# Revit family: 1000811 Font Uber 2 SS Button Tile L&R
name_source: partatom
category: Generic Models
revit_build: Autodesk Revit 2015 (Build: 20160512_1515(x64)
units: mm (PartAtom-declared; Revit-internal decimal feet)

## types (1)
- 1000811 Font Uber 2 SS Button Tile L&R
    Arrangement = Counter Mounted
    AssetType = Fixed
    Color = Brushed Stainless Steel
    ConstructionCasingFinish = Brushed
    ConstructionCasingMaterial = Stainless Steel
    Default Elevation = 1219 mm
    Depth = 360 mm
    Description = Marco Uber style font to be used with Marco Ecoboiler Under counter boilers
    DimensionsDepthMaximum = 470mm
    DimensionsHeightMaximum = 400mm
    DimensionsWidthMaximum = 250mm
    DurationUnit = 5-Years
    ExpectedLife = 5-Years
    H = 272 mm
    Manufacturer = Marco Beverage Systems Ltd.
    Material = Stainless Steel
    ModelNumber = 1000811
    ModelReference = Font Uber 2 SS Button Tile L&R
    Standard = EN 60335-2-75
    ThirdPartyAccreditation = UL, NSF
    URL = http://marcobeveragesystems.com
    WarrantyDescription = Parts Only
    WarrantyDurationLabor = 0
    WarrantyDurationParts = 2-years
    WarrantyDurationUnit = 2-years
    WaterConnections = Marco Uber style font to be used with Marco Ecoboiler Under counter boilers
    Width = 210 mm

## geometry (parser evidence)
native form markers: Blend x4, Sweep x2
no freeform markers — native parametric forms only
